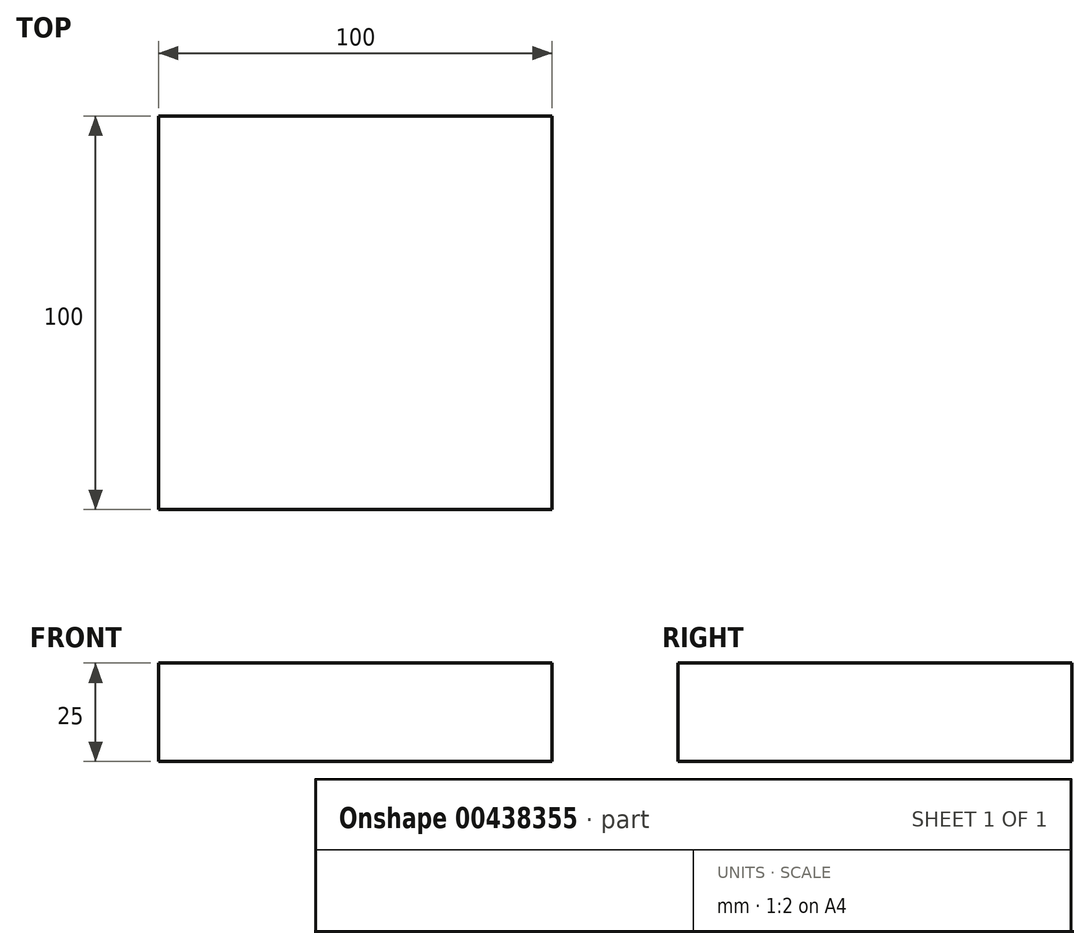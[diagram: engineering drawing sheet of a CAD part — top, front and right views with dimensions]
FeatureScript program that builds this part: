
annotation { "Feature Type Name" : "Feature", "Feature Type Description" : "" }
export const myFeature = defineFeature(function(context is Context, id is Id, definition is map)
    precondition{}
    {
        {
            var Q0;
            Q0=qCreatedBy(makeId("Top.planeOp"),FACE);
            var sketch = newSketch(context, id + "F0", { "sketchPlane" : qUnion([Q0])});
            skLineSegment(sketch, "E0.bottom", {"start": v(0, 0) * mm, "end": v(100, 0) * mm});
            skLineSegment(sketch, "E0.top", {"start": v(0, -100) * mm, "end": v(100, -100) * mm});
            skLineSegment(sketch, "E0.left", {"start": v(0, 0) * mm, "end": v(0, -100) * mm});
            skLineSegment(sketch, "E0.right", {"start": v(100, 0) * mm, "end": v(100, -100) * mm});
            skCircle(sketch, "E1", {"center": v(50, -50) * mm, "radius": 2.5 * mm});
            skPoint(sketch, "E1.centerSnap0", {"position": v(100, -50) * mm});
            skPoint(sketch, "E1.centerSnap1", {"position": v(50, 0) * mm});
            skSolve(sketch);
        }
        {
            var Q0;
            Q0=makeQuery(id+"F0.imprint","IMPRINT",FACE,{"disambiguationData":[TD([[makeQuery(id+"F0.imprint","IMPRINT",EDGE,{"derivedFrom":sQuery(id+"F0.wireOp",EDGE,"E0.bottom")}),-1.0]])]});
            var Q1;
            Q1=makeQuery(id+"F0.imprint","IMPRINT",FACE,{"disambiguationData":[TD([[makeQuery(id+"F0.imprint","IMPRINT",EDGE,{"derivedFrom":sQuery(id+"F0.wireOp",EDGE,"E1")}),1.0]])]});
            extrude(context, id + "F1", {"entities" : qUnion([Q0, Q1]), "depth" : 25 * mm});
        }
    });
